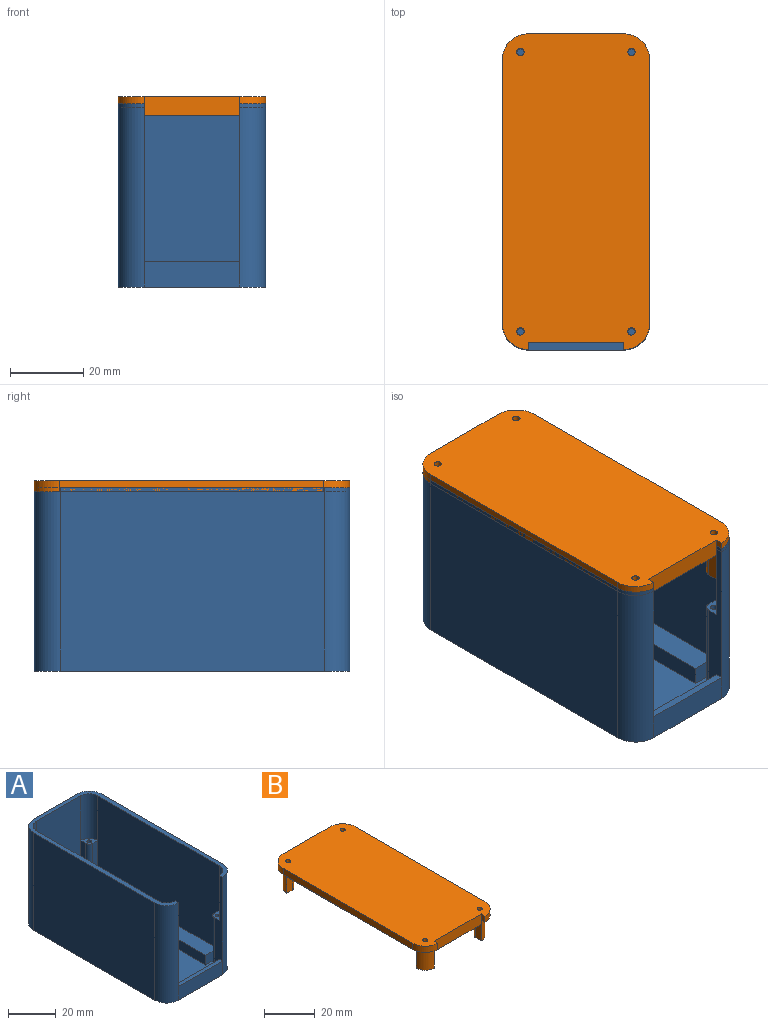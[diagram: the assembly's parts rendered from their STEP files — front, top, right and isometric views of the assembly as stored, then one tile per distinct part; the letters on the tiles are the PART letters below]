
ASSEMBLY  parts=2 mates=1
PART A: 79 faces, bbox 40.1x86x50 mm
  f0: cylinder r=1.27mm len=6mm, axis (0,0,-1), area 47.9mm2, adj f2,f3
  f1: cylinder r=2.27mm len=4.54mm, axis (0,0,-1), area 57.1mm2, adj f3,f36
  f2: plane 86x40.12mm, normal (0,0,-1), area 3082.6mm2, adj f0,f4,f7,f10,f13,f18,f21,f22
  f3: plane 4.54x4.54mm, normal (0,0,1), area 11.1mm2, adj f0,f1
  f4: cylinder r=1.27mm len=6mm, axis (0,0,-1), area 47.9mm2, adj f2,f6
  f5: cylinder r=2.27mm len=4.54mm, axis (0,0,-1), area 57.1mm2, adj f6,f36
  f6: plane 4.54x4.54mm, normal (0,0,1), area 11.1mm2, adj f4,f5
  f7: cylinder r=1.27mm len=6mm, axis (0,0,-1), area 47.9mm2, adj f2,f9
  f8: cylinder r=2.27mm len=4.54mm, axis (0,0,-1), area 57.1mm2, adj f9,f36
  f9: plane 4.54x4.54mm, normal (0,0,1), area 11.1mm2, adj f7,f8
  f10: cylinder r=1.27mm len=6mm, axis (0,0,-1), area 47.9mm2, adj f2,f12
  f11: cylinder r=2.27mm len=4.54mm, axis (0,0,-1), area 57.1mm2, adj f12,f36
  f12: plane 4.54x4.54mm, normal (0,0,1), area 11.1mm2, adj f10,f11
  f13: cylinder r=1.27mm len=6mm, axis (0,0,-1), area 47.9mm2, adj f2,f15
  f14: cylinder r=2.27mm len=4.54mm, axis (0,0,-1), area 57.1mm2, adj f15,f36
  f15: plane 4.54x4.54mm, normal (0,0,1), area 11.1mm2, adj f13,f14
  f16: cylinder r=5mm len=23mm, axis (0,0,-1), area 180.6mm2, adj f20,f28,f29,f51
  f17: cylinder r=5mm len=23mm, axis (0,0,-1), area 180.6mm2, adj f20,f31,f35,f56
  f18: plane 26.12x7mm, normal (0,-1,0), area 182.8mm2, adj f2,f24,f25,f33
  f19: plane 26.12x5mm, normal (0,1,0), area 130.6mm2, adj f33,f34,f35,f36
  f20: plane 86x40.12mm, normal (0,0,1), area 415.6mm2, adj f16,f17,f21,f22,f23,f24,f25,f26
  f21: plane 50x26.12mm, normal (0,1,0), area 1305.8mm2, adj f2,f20,f22,f32
  f22: cylinder r=7mm len=50mm, axis (0,0,-1), area 549.8mm2, adj f2,f20,f21,f23
  f23: plane 72x50mm, normal (-1,0,0), area 3600mm2, adj f2,f20,f22,f24
  f24: cylinder r=7mm len=50mm, axis (0,0,-1), area 549.8mm2, adj f2,f18,f20,f23,f35
  f25: cylinder r=7mm len=50mm, axis (0,0,-1), area 549.8mm2, adj f2,f18,f20,f26,f34
  f26: plane 72x50mm, normal (1,0,0), area 3600mm2, adj f2,f20,f25,f32
  f27: cylinder r=5mm len=23mm, axis (0,0,-1), area 180.6mm2, adj f20,f28,f31,f45
  f28: plane 48x26.12mm, normal (0,-1,0), area 1253.6mm2, adj f16,f20,f27,f36,f41,f47
  f29: plane 72x48mm, normal (-1,0,0), area 3221mm2, adj f16,f20,f30,f36,f48,f58,f67,f69
  f30: cylinder r=5mm len=23mm, axis (0,0,-1), area 180.6mm2, adj f20,f29,f34,f61
  f31: plane 72x48mm, normal (1,0,0), area 3221mm2, adj f17,f20,f27,f36,f42,f53,f63,f64
  f32: cylinder r=7mm len=50mm, axis (0,0,-1), area 549.8mm2, adj f2,f20,f21,f26
  f33: plane 26.12x2mm, normal (0,0,1), area 52.2mm2, adj f18,f19,f34,f35
  f34: plane 48x4.93mm, normal (-1,0,0), area 159.2mm2, adj f19,f20,f25,f30,f33,f36,f60,f61
  f35: plane 48x4.93mm, normal (1,0,0), area 159.2mm2, adj f17,f19,f20,f24,f33,f36,f55,f56
  f36: plane 82x36.12mm, normal (0,0,1), area 1826.3mm2, adj f1,f5,f8,f11,f14,f19,f28,f29
  f37: plane 15x2mm, normal (-1,0,0), area 30mm2, adj f2,f36,f38,f40
  f38: plane 20x2mm, normal (0,1,0), area 40mm2, adj f2,f36,f37,f39
  f39: plane 15x2mm, normal (1,0,0), area 30mm2, adj f2,f36,f38,f40
  f40: plane 20x2mm, normal (0,-1,0), area 40mm2, adj f2,f36,f37,f39
  f41: plane 25x2.93mm, normal (1,0,0), area 73.2mm2, adj f28,f36,f44,f45
  f42: plane 25x2.93mm, normal (0,-1,0), area 73.2mm2, adj f31,f36,f44,f45
  f43: cylinder r=1mm len=25mm, axis (0,0,-1), area 157.1mm2, adj f45,f46
  f44: cylinder r=2.07mm len=25mm, axis (0,0,-1), area 81.3mm2, adj f36,f41,f42,f45
  f45: plane 5x5mm, normal (0,0,1), area 15.6mm2, adj f27,f41,f42,f43,f44
  f46: plane 2x2mm, normal (0,0,1), area 3.1mm2, adj f43
  f47: plane 25x2.93mm, normal (-1,0,0), area 73.2mm2, adj f28,f36,f50,f51
  f48: plane 25x2.93mm, normal (0,-1,0), area 73.2mm2, adj f29,f36,f50,f51
  f49: cylinder r=1mm len=25mm, axis (0,0,-1), area 157.1mm2, adj f51,f52
  f50: cylinder r=2.07mm len=25mm, axis (0,0,-1), area 81.3mm2, adj f36,f47,f48,f51
  f51: plane 5x5mm, normal (0,0,1), area 15.6mm2, adj f16,f47,f48,f49,f50
  f52: plane 2x2mm, normal (0,0,1), area 3.1mm2, adj f49
  f53: plane 25x2.93mm, normal (0,1,0), area 73.2mm2, adj f31,f36,f55,f56
  f54: cylinder r=1mm len=25mm, axis (0,0,-1), area 157.1mm2, adj f56,f57
  f55: cylinder r=2.07mm len=25mm, axis (0,0,-1), area 81.3mm2, adj f35,f36,f53,f56
  f56: plane 5x5mm, normal (0,0,1), area 15.6mm2, adj f17,f35,f53,f54,f55
  f57: plane 2x2mm, normal (0,0,1), area 3.1mm2, adj f54
  f58: plane 25x2.93mm, normal (0,1,0), area 73.2mm2, adj f29,f36,f60,f61
  f59: cylinder r=1mm len=25mm, axis (0,0,-1), area 157.1mm2, adj f61,f62
  f60: cylinder r=2.07mm len=25mm, axis (0,0,-1), area 81.3mm2, adj f34,f36,f58,f61
  f61: plane 5x5mm, normal (0,0,1), area 15.6mm2, adj f30,f34,f58,f59,f60
  f62: plane 2x2mm, normal (0,0,1), area 3.1mm2, adj f59
  f63: plane 7x5mm, normal (0,1,0), area 35mm2, adj f31,f36,f65,f66
  f64: plane 7x5mm, normal (0,-1,0), area 35mm2, adj f31,f36,f65,f66
  f65: plane 35x5mm, normal (1,0,0), area 175mm2, adj f36,f63,f64,f66
  f66: plane 35x7mm, normal (0,0,1), area 245mm2, adj f31,f63,f64,f65
  f67: plane 7x5mm, normal (0,1,0), area 35mm2, adj f29,f36,f68,f70
  f68: plane 35x5mm, normal (-1,0,0), area 175mm2, adj f36,f67,f69,f70
  f69: plane 7x5mm, normal (0,-1,0), area 35mm2, adj f29,f36,f68,f70
  f70: plane 35x7mm, normal (0,0,1), area 245mm2, adj f29,f67,f68,f69
  f71: plane 7x5mm, normal (0,1,0), area 35mm2, adj f29,f36,f72,f74
  f72: plane 12x5mm, normal (-1,0,0), area 60mm2, adj f36,f71,f73,f74
  f73: plane 7x5mm, normal (0,-1,0), area 35mm2, adj f29,f36,f72,f74
  f74: plane 12x7mm, normal (0,0,1), area 84mm2, adj f29,f71,f72,f73
  f75: plane 7x5mm, normal (0,-1,0), area 35mm2, adj f31,f36,f76,f78
  f76: plane 12x5mm, normal (1,0,0), area 60mm2, adj f36,f75,f77,f78
  f77: plane 7x5mm, normal (0,1,0), area 35mm2, adj f31,f36,f76,f78
  f78: plane 12x7mm, normal (0,0,1), area 84mm2, adj f31,f75,f76,f77
PART B: 40 faces, bbox 40.1x86x13 mm
  f0: plane 72x2mm, normal (-1,0,0), area 144mm2, adj f4,f14,f20,f29
  f1: plane 26.12x5mm, normal (0,-1,0), area 130.6mm2, adj f4,f8,f14,f30,f38,f39
  f2: plane 72x2mm, normal (1,0,0), area 144mm2, adj f4,f8,f26,f29
  f3: plane 26.12x2mm, normal (0,1,0), area 52.2mm2, adj f4,f20,f26,f29
  f4: plane 82x36.12mm, normal (0,0,-1), area 2865.2mm2, adj f0,f1,f2,f3,f5,f6,f7,f11
  f5: plane 8x2.93mm, normal (-1,0,0), area 23.4mm2, adj f4,f7,f8,f10
  f6: plane 8x2.93mm, normal (0,1,0), area 23.4mm2, adj f4,f7,f8,f10
  f7: cylinder r=2.07mm len=8mm, axis (0,0,1), area 26mm2, adj f4,f5,f6,f10
  f8: cylinder r=5mm len=10mm, axis (0,0,1), area 78.5mm2, adj f1,f2,f5,f6,f10,f29
  f9: cylinder r=1mm len=13mm, axis (0,0,1), area 81.7mm2, adj f10,f39
  f10: plane 5x5mm, normal (0,0,-1), area 15.6mm2, adj f5,f6,f7,f8,f9
  f11: plane 8x2.93mm, normal (0,1,0), area 23.4mm2, adj f4,f13,f14,f16
  f12: plane 8x2.93mm, normal (1,0,0), area 23.4mm2, adj f4,f13,f14,f16
  f13: cylinder r=2.07mm len=8mm, axis (0,0,1), area 26mm2, adj f4,f11,f12,f16
  f14: cylinder r=5mm len=10mm, axis (0,0,1), area 78.5mm2, adj f0,f1,f11,f12,f16,f29
  f15: cylinder r=1mm len=13mm, axis (0,0,1), area 81.7mm2, adj f16,f39
  f16: plane 5x5mm, normal (0,0,-1), area 15.6mm2, adj f11,f12,f13,f14,f15
  f17: plane 8x2.93mm, normal (1,0,0), area 23.4mm2, adj f4,f19,f20,f22
  f18: plane 8x2.93mm, normal (0,-1,0), area 23.4mm2, adj f4,f19,f20,f22
  f19: cylinder r=2.07mm len=8mm, axis (0,0,1), area 26mm2, adj f4,f17,f18,f22
  f20: cylinder r=5mm len=10mm, axis (0,0,1), area 78.5mm2, adj f0,f3,f17,f18,f22,f29
  f21: cylinder r=1mm len=13mm, axis (0,0,1), area 81.7mm2, adj f22,f39
  f22: plane 5x5mm, normal (0,0,-1), area 15.6mm2, adj f17,f18,f19,f20,f21
  f23: plane 8x2.93mm, normal (-1,0,0), area 23.4mm2, adj f4,f25,f26,f28
  f24: plane 8x2.93mm, normal (0,-1,0), area 23.4mm2, adj f4,f25,f26,f28
  f25: cylinder r=2.07mm len=8mm, axis (0,0,1), area 26mm2, adj f4,f23,f24,f28
  f26: cylinder r=5mm len=10mm, axis (0,0,1), area 78.5mm2, adj f2,f3,f23,f24,f28,f29
  f27: cylinder r=1mm len=13mm, axis (0,0,1), area 81.7mm2, adj f28,f39
  f28: plane 5x5mm, normal (0,0,-1), area 15.6mm2, adj f23,f24,f25,f26,f27
  f29: plane 86x40.12mm, normal (0,0,-1), area 415.6mm2, adj f0,f2,f3,f8,f14,f20,f26,f30
  f30: plane 3x2mm, normal (-1,0,0), area 6mm2, adj f1,f29,f31,f39
  f31: cylinder r=7mm len=7mm, axis (0,0,-1), area 33mm2, adj f29,f30,f32,f39
  f32: plane 72x3mm, normal (1,0,0), area 216mm2, adj f29,f31,f33,f39
  f33: cylinder r=7mm len=7mm, axis (0,0,-1), area 33mm2, adj f29,f32,f34,f39
  f34: plane 26.12x3mm, normal (0,1,0), area 78.3mm2, adj f29,f33,f35,f39
  f35: cylinder r=7mm len=7mm, axis (0,0,-1), area 33mm2, adj f29,f34,f36,f39
  f36: plane 72x3mm, normal (-1,0,0), area 216mm2, adj f29,f35,f37,f39
  f37: cylinder r=7mm len=7mm, axis (0,0,-1), area 33mm2, adj f29,f36,f38,f39
  f38: plane 3x2mm, normal (1,0,0), area 6mm2, adj f1,f29,f37,f39
  f39: plane 86x40.12mm, normal (0,0,1), area 3343.1mm2, adj f1,f9,f15,f21,f27,f30,f31,f32
PLACE A t=(-43.9,2.67,-54.48)mm
PLACE B t=(-43.9,2.76,-105.68)mm
MATE parallel B.f4 <-> A.f36  axis (0,0,-1) through (-43.9,2.76,-7.68)mm
